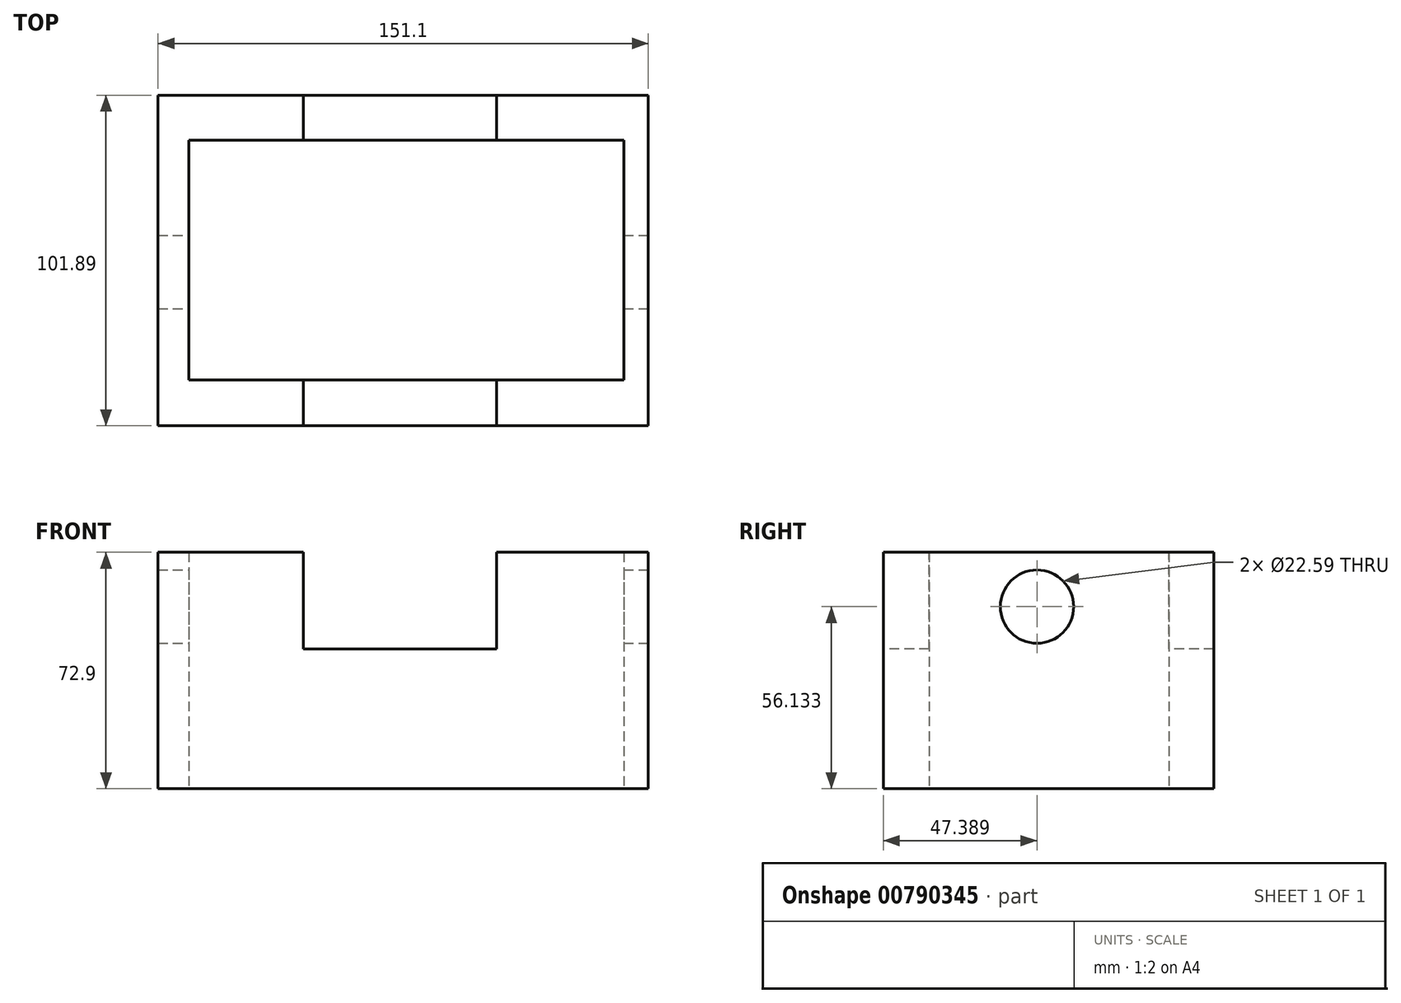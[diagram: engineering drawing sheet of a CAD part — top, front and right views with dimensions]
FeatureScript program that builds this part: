
annotation { "Feature Type Name" : "Feature", "Feature Type Description" : "" }
export const myFeature = defineFeature(function(context is Context, id is Id, definition is map)
    precondition{}
    {
        {
            var Q0;
            Q0=qCreatedBy(makeId("Top.planeOp"),FACE);
            var sketch = newSketch(context, id + "F0", { "sketchPlane" : qUnion([Q0])});
            skLineSegment(sketch, "E0.bottom", {"start": v(-76.1, -41.78) * mm, "end": v(75, -41.78) * mm});
            skLineSegment(sketch, "E0.top", {"start": v(-76.1, 60.11) * mm, "end": v(75, 60.11) * mm});
            skLineSegment(sketch, "E0.left", {"start": v(-76.1, -41.78) * mm, "end": v(-76.1, 60.11) * mm});
            skLineSegment(sketch, "E0.right", {"start": v(75, -41.78) * mm, "end": v(75, 60.11) * mm});
            skLineSegment(sketch, "E1.bottom", {"start": v(-66.58, -27.66) * mm, "end": v(67.47, -27.66) * mm});
            skLineSegment(sketch, "E1.top", {"start": v(-66.58, 46.28) * mm, "end": v(67.47, 46.28) * mm});
            skLineSegment(sketch, "E1.left", {"start": v(-66.58, -27.66) * mm, "end": v(-66.58, 46.28) * mm});
            skLineSegment(sketch, "E1.right", {"start": v(67.47, -27.66) * mm, "end": v(67.47, 46.28) * mm});
            skSolve(sketch);
        }
        {
            var Q0;
            Q0=makeQuery(id+"F0.imprint","IMPRINT",FACE,{"disambiguationData":[TD([[makeQuery(id+"F0.imprint","IMPRINT",EDGE,{"derivedFrom":sQuery(id+"F0.wireOp",EDGE,"E0.bottom")}),1.0]])]});
            extrude(context, id + "F1", {"entities" : qUnion([Q0]), "depth" : 72.9 * mm, "offsetDistance" : 25.4 * mm});
        }
        {
            var Q0;
            Q0=makeQuery(id+"F1.opExtrude","SWEPT_FACE",FACE,{"disambiguationData":[OSD([sQuery(id+"F0.wireOp",EDGE,"E0.bottom")])]});
            var sketch = newSketch(context, id + "F2", { "sketchPlane" : qUnion([Q0])});
            skLineSegment(sketch, "E2.bottom", {"start": v(-31.27, 72.9) * mm, "end": v(28.22, 72.9) * mm});
            skLineSegment(sketch, "E2.top", {"start": v(-31.27, 43.05) * mm, "end": v(28.22, 43.05) * mm});
            skLineSegment(sketch, "E2.left", {"start": v(-31.27, 72.9) * mm, "end": v(-31.27, 43.05) * mm});
            skLineSegment(sketch, "E2.right", {"start": v(28.22, 72.9) * mm, "end": v(28.22, 43.05) * mm});
            skSolve(sketch);
        }
        {
            var Q0;
            Q0=makeQuery(id+"F2.imprint","IMPRINT",FACE,{"disambiguationData":[TD([[makeQuery(id+"F2.imprint","IMPRINT",EDGE,{"derivedFrom":sQuery(id+"F2.wireOp",EDGE,"E2.bottom")}),-1.0]])]});
            extrude(context, id + "F3", {"entities" : qUnion([Q0]), "operationType" : NewBodyOperationType.REMOVE, "oppositeDirection" : true, "depth" : 161.29 * mm, "offsetDistance" : 25.4 * mm});
        }
        {
            var Q0;
            Q0=makeQuery(id+"F1.opExtrude","SWEPT_FACE",FACE,{"disambiguationData":[OSD([sQuery(id+"F0.wireOp",EDGE,"E0.right")])]});
            var sketch = newSketch(context, id + "F4", { "sketchPlane" : qUnion([Q0])});
            skCircle(sketch, "E3", {"center": v(5.6, 56.13) * mm, "radius": 11.3 * mm});
            skSolve(sketch);
        }
        {
            var Q0;
            Q0=makeQuery(id+"F4.imprint","IMPRINT",FACE,{"disambiguationData":[TD([[makeQuery(id+"F4.imprint","IMPRINT",EDGE,{"derivedFrom":sQuery(id+"F4.wireOp",EDGE,"E3")}),1.0]])]});
            extrude(context, id + "F5", {"entities" : qUnion([Q0]), "operationType" : NewBodyOperationType.REMOVE, "oppositeDirection" : true, "depth" : 227.84 * mm, "offsetDistance" : 25.4 * mm});
        }
    });
